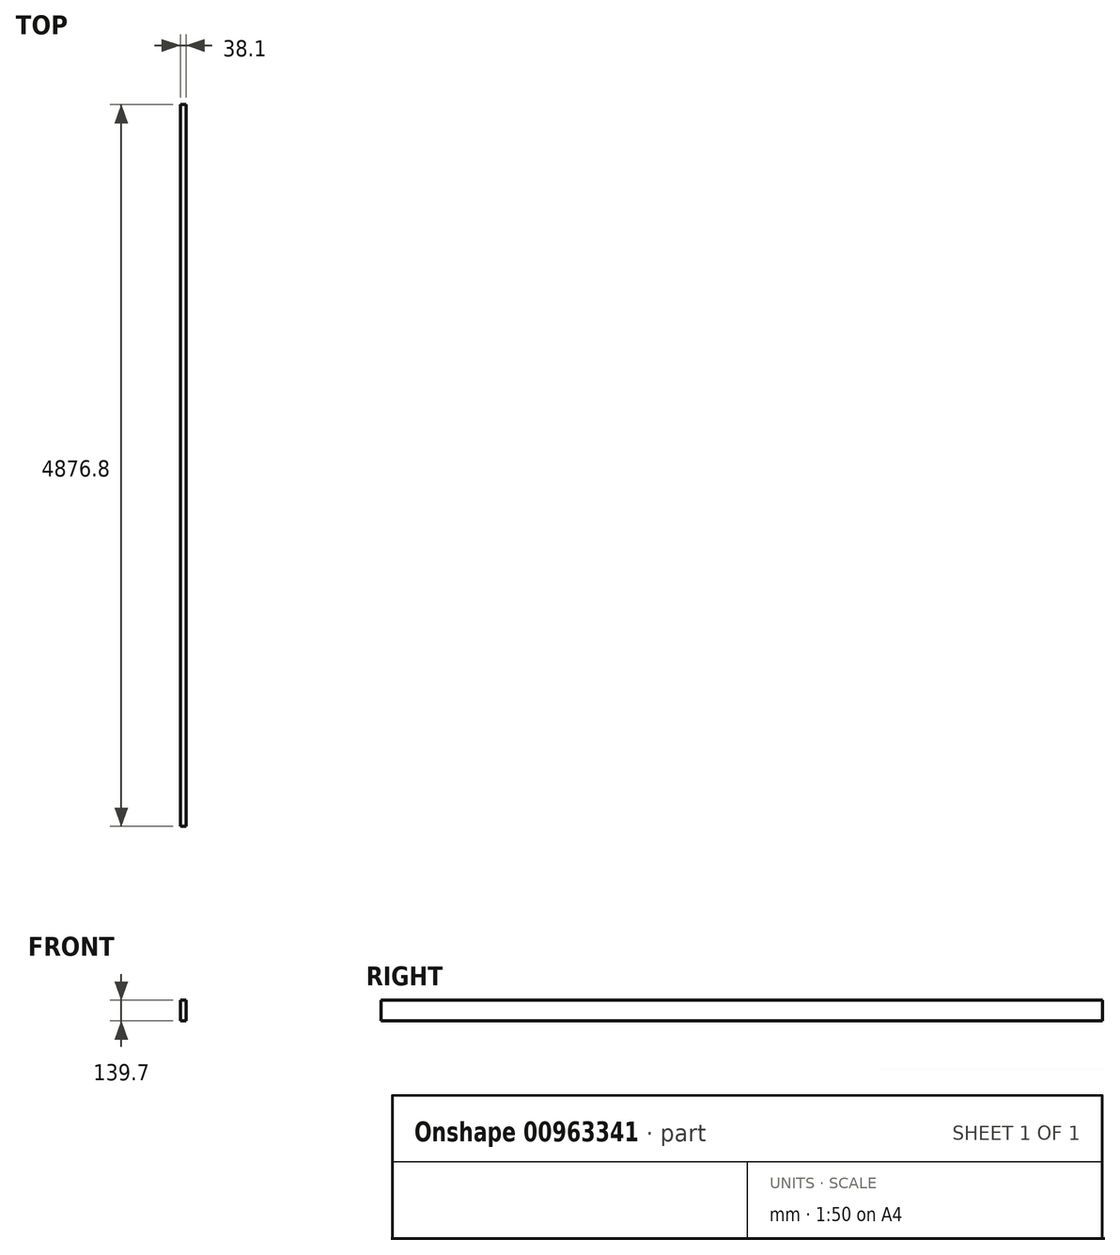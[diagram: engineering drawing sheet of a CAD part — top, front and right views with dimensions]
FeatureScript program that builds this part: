
annotation { "Feature Type Name" : "Feature", "Feature Type Description" : "" }
export const myFeature = defineFeature(function(context is Context, id is Id, definition is map)
    precondition{}
    {
        {
            var Q0;
            Q0=qCreatedBy(makeId("Front.planeOp"),FACE);
            var sketch = newSketch(context, id + "F0", { "sketchPlane" : qUnion([Q0])});
            skLineSegment(sketch, "E0.bottom", {"start": v(0, 0) * mm, "end": v(38.1, 0) * mm});
            skLineSegment(sketch, "E0.top", {"start": v(0, 139.7) * mm, "end": v(38.1, 139.7) * mm});
            skLineSegment(sketch, "E0.left", {"start": v(0, 0) * mm, "end": v(0, 139.7) * mm});
            skLineSegment(sketch, "E0.right", {"start": v(38.1, 0) * mm, "end": v(38.1, 139.7) * mm});
            skSolve(sketch);
        }
        {
            var Q0;
            Q0=makeQuery(id+"F0.imprint","IMPRINT",FACE,{"disambiguationData":[TD([[makeQuery(id+"F0.imprint","IMPRINT",EDGE,{"derivedFrom":sQuery(id+"F0.wireOp",EDGE,"E0.bottom")}),1.0]])]});
            extrude(context, id + "F1", {"entities" : qUnion([Q0]), "offsetDistance" : 25.4 * mm, "depth" : 4876.8 * mm});
        }
    });
